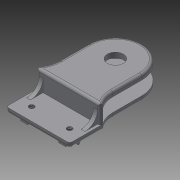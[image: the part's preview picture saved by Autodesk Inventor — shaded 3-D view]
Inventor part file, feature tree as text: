
AUTODESK INVENTOR PART (.ipt)
format: ipt  version: 2013 (Build 170138000, 138)  size: 345,088 bytes
history: native  units: mm
features: extrude x8, sketch x8, fillet x4, hole x1, chamfer x1, mirror x1
ambient origin geometry x8: Origin, YZ Plane, XZ Plane, XY Plane, X Axis, Y Axis, Z Axis, Center Point
bodies: Solid1 (feature_tree)
feature tree (23):
  extrude  "Extrusion1"  Depth=17.5mm
  sketch  "Sketch2"  dims[d3=6.35mm d4=10.5mm]
  extrude  "Extrusion2"  Depth=10.5mm
  extrude  "Extrusion3"  Depth=2.0mm
  extrude  "Extrusion4"  Depth=25.0mm
  sketch  "Sketch6"  dims[d12=1.0mm d13=0.0mm d14=2.0mm]
  hole  "Hole1"  [1 undecoded]
  extrude  "Extrusion5"  Depth=5.0mm
  extrude  "Extrusion6"  Depth=5.0mm
  extrude  "Extrusion7"  Depth=1.0mm TaperAngle=0.0deg
  chamfer  "Chamfer1"  Distance=0.5mm
  mirror  "Mirror1"
  fillet  "Fillet1"  Radius=1.0mm
  fillet  "Fillet2"  Radius=1.0mm
  fillet  "Fillet3"  Radius=1.0mm
  extrude  "Extrusion8"  Depth=1.0mm TaperAngle=45.0deg
  fillet  "Fillet4"  Radius=10.5mm
  sketch  "Sketch1"  dims[d0=21.0mm d2=17.5mm]
  sketch  "Sketch3"  dims[d5=9.35mm d6=0.0mm d7=2.0mm]
  sketch  "Sketch4"  dims[d8=2.0mm d9=0.0mm d10=25.0mm]
  sketch  "Sketch7"  dims[d16=12.0mm d17=0.0mm d18=5.0mm]
  sketch  "Sketch8"  dims[d19=5.0mm d20=5.0mm]
  sketch  "Sketch9"  dims[d21=2.013mm d22=6.0mm d23=3.023mm d24=2.0mm d25=14.3117mm d26=8.0mm d27=20.594885mm d28=1.0mm d29=0.0mm d30=0.5mm d31=1.0mm d32=0.0mm d33=1.0mm d34=1.0mm d35=0.0mm d36=1.0mm d37=2.0mm d38=45.0deg d39=10.5mm d40=10.0mm d41=5.0mm d43=1.5mm d45=1.0mm d46=1.0mm d47=0.0mm d48=1.0mm]
note: 1 required parameter value undecoded (feature->parameter linkage not recoverable at this tier; creation-order binding heuristic only, values carry confidence <= 0.55)
